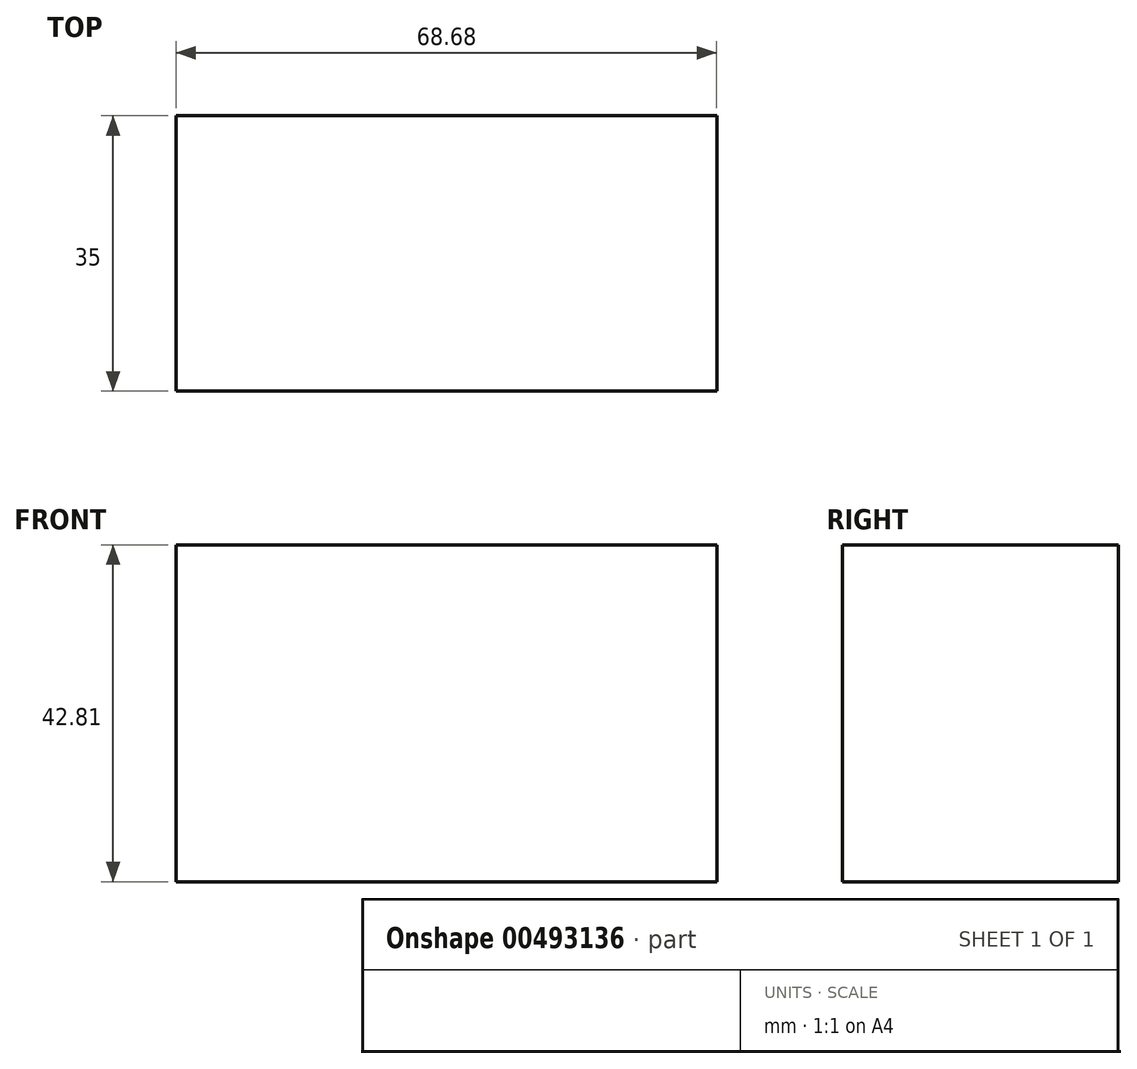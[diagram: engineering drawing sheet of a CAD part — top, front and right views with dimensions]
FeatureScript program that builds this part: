
annotation { "Feature Type Name" : "Feature", "Feature Type Description" : "" }
export const myFeature = defineFeature(function(context is Context, id is Id, definition is map)
    precondition{}
    {
        {
            var Q0;
            Q0=qCreatedBy(makeId("Front.planeOp"),FACE);
            var sketch = newSketch(context, id + "F0", { "sketchPlane" : qUnion([Q0])});
            skLineSegment(sketch, "E0.bottom", {"start": v(-34.18, 20.93) * mm, "end": v(34.5, 20.93) * mm});
            skLineSegment(sketch, "E0.top", {"start": v(-34.18, -21.88) * mm, "end": v(34.5, -21.88) * mm});
            skLineSegment(sketch, "E0.left", {"start": v(-34.18, 20.93) * mm, "end": v(-34.18, -21.88) * mm});
            skLineSegment(sketch, "E0.right", {"start": v(34.5, 20.93) * mm, "end": v(34.5, -21.88) * mm});
            skSolve(sketch);
        }
        {
            var Q0;
            Q0=qSketchRegion(id+"F0",true);
            extrude(context, id + "F1", {"entities" : qUnion([Q0]), "endBound" : BoundingType.SYMMETRIC, "depth" : 35 * mm, "offsetDistance" : 25 * mm});
        }
    });
